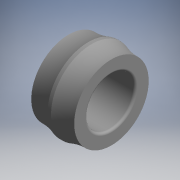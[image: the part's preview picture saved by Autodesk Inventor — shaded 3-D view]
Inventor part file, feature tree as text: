
AUTODESK INVENTOR PART (.ipt)
format: ipt  version: 2017.3 (Build 213256000, 256)  size: 156,160 bytes
history: native  units: mm (DEFAULTED — no unit token found)
features: other x14, revolve x1, sketch x1
ambient origin geometry x8: Origin, YZ Plane, XZ Plane, XY Plane, X Axis, Y Axis, Z Axis, Center Point
bodies: Solid1 (feature_tree)
feature tree (16):
  revolve  "Revolution1"  [1 undecoded]
  other  "NO_GEO_XY"
  other  "NO_GEO_YZ"
  other  "NO_GEO_ZX"
  other  "NO_GEO_X"
  other  "NO_GEO_Y"
  other  "NO_GEO_Z"
  other  "NO_GEO_Center"
  other  "ir_XY"
  other  "ir_YZ"
  other  "ir_ZX"
  other  "ir_X"
  other  "ir_Y"
  other  "ir_Z"
  other  "ir_Center"
  sketch  "Sketch_1"  dims[d0=360.0deg d1=0.0mm]
note: 1 required parameter value undecoded (feature->parameter linkage not recoverable at this tier; creation-order binding heuristic only, values carry confidence <= 0.55)
